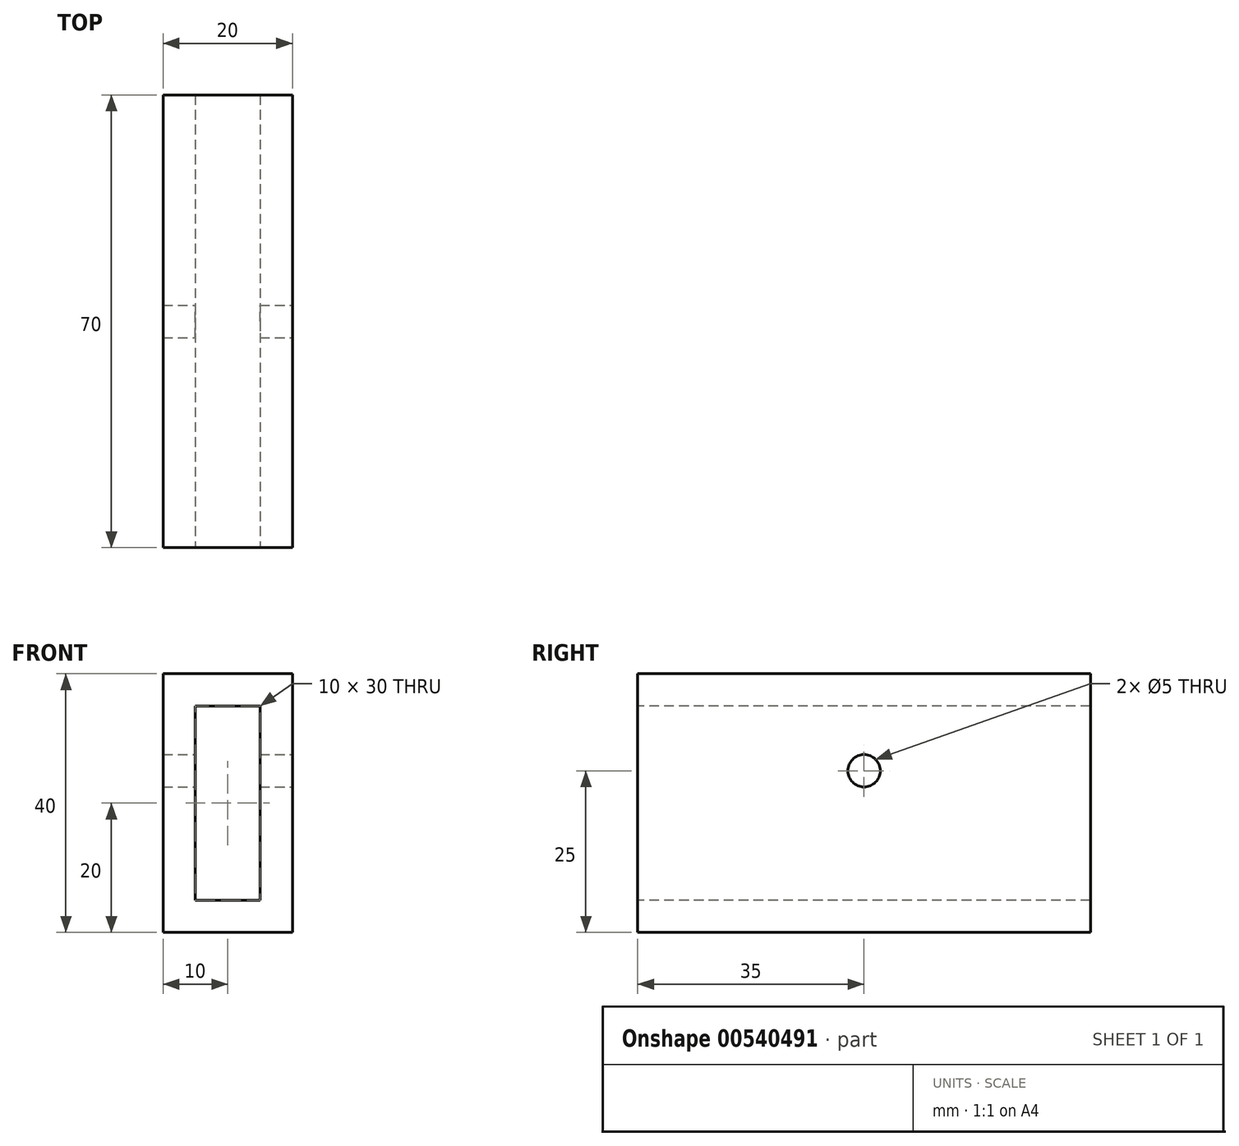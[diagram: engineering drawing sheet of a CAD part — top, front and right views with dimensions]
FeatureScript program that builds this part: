
annotation { "Feature Type Name" : "Feature", "Feature Type Description" : "" }
export const myFeature = defineFeature(function(context is Context, id is Id, definition is map)
    precondition{}
    {
        {
            var Q0;
            Q0=qCreatedBy(makeId("Front.planeOp"),FACE);
            var sketch = newSketch(context, id + "F0", { "sketchPlane" : qUnion([Q0])});
            skLineSegment(sketch, "E0.bottom", {"start": v(0, 0) * mm, "end": v(20, 0) * mm});
            skLineSegment(sketch, "E0.top", {"start": v(0, 40) * mm, "end": v(20, 40) * mm});
            skLineSegment(sketch, "E0.left", {"start": v(0, 0) * mm, "end": v(0, 40) * mm});
            skLineSegment(sketch, "E0.right", {"start": v(20, 0) * mm, "end": v(20, 40) * mm});
            skSolve(sketch);
        }
        {
            var Q0;
            Q0 = qSketchRegion(id + "F0", true);
            extrude(context, id + "F1", {"entities" : qUnion([Q0]), "depth" : 70 * mm, "offsetDistance" : 25 * mm});
        }
        {
            var Q0;
            Q0=makeQuery(id+"F1.opExtrude","SWEPT_FACE",FACE,{"disambiguationData":[OSD([sQuery(id+"F0.wireOp",EDGE,"E0.right")])]});
            var sketch = newSketch(context, id + "F2", { "sketchPlane" : qUnion([Q0])});
            skCircle(sketch, "E1", {"center": v(-35, 25) * mm, "radius": 2.5 * mm});
            skPoint(sketch, "E2", {"position": v(-35, 40) * mm});
            skSolve(sketch);
        }
        {
            var Q0;
            Q0 = qSketchRegion(id + "F2", true);
            extrude(context, id + "F3", {"entities" : qUnion([Q0]), "operationType" : NewBodyOperationType.REMOVE, "endBound" : BoundingType.THROUGH_ALL, "oppositeDirection" : true, "depth" : 25 * mm, "offsetDistance" : 25 * mm});
        }
        {
            var Q0;
            Q0=makeQuery(id+"F1.opExtrude","CAP_FACE",FACE,{"disambiguationData":[OSD([sQuery(id+"F0.wireOp",EDGE,"E0.bottom"),sQuery(id+"F0.wireOp",EDGE,"E0.top"),sQuery(id+"F0.wireOp",EDGE,"E0.left"),sQuery(id+"F0.wireOp",EDGE,"E0.right")])],"isStart":false});
            var sketch = newSketch(context, id + "F4", { "sketchPlane" : qUnion([Q0])});
            skLineSegment(sketch, "E3.bottom", {"start": v(5, 35) * mm, "end": v(15, 35) * mm});
            skLineSegment(sketch, "E3.top", {"start": v(5, 5) * mm, "end": v(15, 5) * mm});
            skLineSegment(sketch, "E3.left", {"start": v(5, 35) * mm, "end": v(5, 5) * mm});
            skLineSegment(sketch, "E3.right", {"start": v(15, 35) * mm, "end": v(15, 5) * mm});
            skPoint(sketch, "E4", {"position": v(10, 35) * mm});
            skPoint(sketch, "E5", {"position": v(10, 40) * mm});
            skPoint(sketch, "E6", {"position": v(15, 20) * mm});
            skPoint(sketch, "E7", {"position": v(20, 20) * mm});
            skSolve(sketch);
        }
        {
            var Q0;
            Q0=makeQuery(id+"F4.imprint","IMPRINT",FACE,{"disambiguationData":[TD([[makeQuery(id+"F4.imprint","IMPRINT",EDGE,{"derivedFrom":sQuery(id+"F4.wireOp",EDGE,"E3.bottom")}),-1.0]])]});
            extrude(context, id + "F5", {"entities" : qUnion([Q0]), "operationType" : NewBodyOperationType.REMOVE, "endBound" : BoundingType.THROUGH_ALL, "oppositeDirection" : true, "depth" : 25 * mm, "offsetDistance" : 25 * mm});
        }
    });
